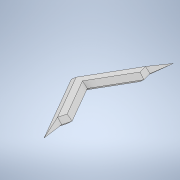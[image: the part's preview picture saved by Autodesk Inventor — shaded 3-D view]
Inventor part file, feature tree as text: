
AUTODESK INVENTOR PART (.ipt)
format: ipt  version: 2020 (Build 240168000, 168)  size: 135,680 bytes
history: native  units: mm
features: chamfer x4, extrude x1, sketch x1
ambient origin geometry x8: Origin, YZ Plane, XZ Plane, XY Plane, X Axis, Y Axis, Z Axis, Center Point
bodies: Solid1 (feature_tree)
feature tree (6):
  extrude  "Extrusion1"  TaperAngle=0.0deg  [1 undecoded]
  chamfer  "Chamfer1"  [1 undecoded]
  chamfer  "Chamfer2"  Angle=60.0deg  [1 undecoded]
  chamfer  "Chamfer3"  Angle=60.0deg  [1 undecoded]
  chamfer  "Chamfer4"  Distance=5.0mm
  sketch  "Sketch1"  dims[d0=0.0mm d1=0.0mm d2=0.0mm d3=60.0deg d4=60.0deg d5=5.0mm d6=135.0deg d7=135.0deg d8=15.0mm d9=15.0mm d10=3.0mm d11=3.0mm d12=27.0mm d13=27.0mm d14=3.0mm d15=0.0mm d16=1.5mm d17=2.0mm d18=45.0deg d19=1.5mm d20=2.0mm d21=45.0deg d22=1.5mm d23=2.0mm d24=45.0deg d25=1.5mm d26=2.0mm d27=45.0deg]
note: 4 required parameter values undecoded (feature->parameter linkage not recoverable at this tier; creation-order binding heuristic only, values carry confidence <= 0.55)
